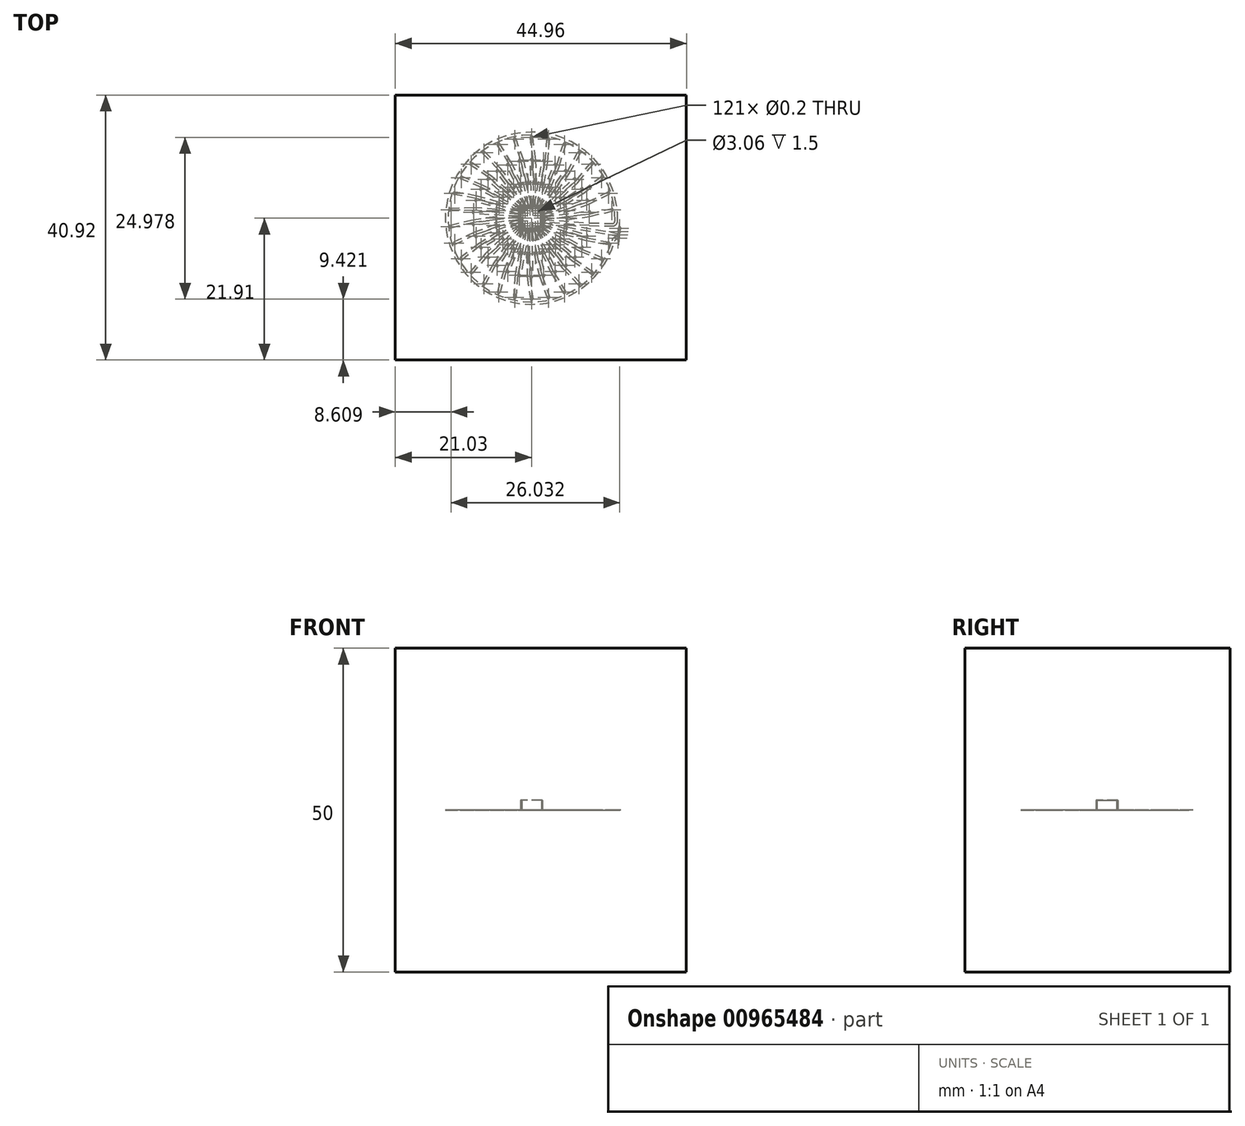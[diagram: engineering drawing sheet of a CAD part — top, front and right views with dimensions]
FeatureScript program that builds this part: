
annotation { "Feature Type Name" : "Feature", "Feature Type Description" : "" }
export const myFeature = defineFeature(function(context is Context, id is Id, definition is map)
    precondition{}
    {
        {
            var Q0;
            Q0=qCreatedBy(makeId("Top.planeOp"), FACE);
            var sketch = newSketch(context, id + "F0", { "sketchPlane" : qUnion([Q0])});
            skLineSegment(sketch, "E0.bottom", {"start": v(-21.03, 19.01) * mm, "end": v(23.93, 19.01) * mm});
            skLineSegment(sketch, "E0.top", {"start": v(-21.03, -21.9) * mm, "end": v(23.93, -21.9) * mm});
            skLineSegment(sketch, "E0.left", {"start": v(-21.03, 19.01) * mm, "end": v(-21.03, -21.9) * mm});
            skLineSegment(sketch, "E0.right", {"start": v(23.93, 19.01) * mm, "end": v(23.93, -21.9) * mm});
            skSolve(sketch);
        }
        {
            var Q0;
            Q0 = qSketchRegion(id + "F0", true);
            extrude(context, id + "F1", {"entities" : qUnion([Q0]), "depth" : 25 * mm, "offsetDistance" : 25 * mm, "hasSecondDirection" : true, "secondDirectionOppositeDirection" : true, "secondDirectionDepth" : 25 * mm});
        }
        {
            assignVariable(context, id + "F2", {"name" : "A", "anyValue" : 12});
        }
        {
            assignVariable(context, id + "F3", {"name" : "ePCB", "anyValue" : 1.5});
        }
        {
            assignVariable(context, id + "F4", {"name" : "eCU", "anyValue" : 0});
        }
        {
            var Q0;
            Q0=qCreatedBy(makeId("Top.planeOp"),FACE);
            var sketch = newSketch(context, id + "F5", { "sketchPlane" : qUnion([Q0])});
            skCircle(sketch, "E1", {"center": v(2, 0) * mm, "radius": 0.1 * mm});
            skCircle(sketch, "E2.1.0", {"center": v(1.96, 0.42) * mm, "radius": 0.1 * mm});
            skPoint(sketch, "E2.center", {"position": v(0, 0) * mm});
            skLineSegment(sketch, "E2.anchor1", {"start": v(0, 0) * mm, "end": v(2, 0) * mm, "construction": true});
            skLineSegment(sketch, "E2.anchor2", {"start": v(0, 0) * mm, "end": v(1.96, 0.42) * mm, "construction": true});
            skLineSegment(sketch, "E3", {"start": v(1.96, 0.42) * mm, "end": v(2, 0) * mm, "construction": true});
            skLineSegment(sketch, "E4", {"start": v(0, 0) * mm, "end": v(1.98, 0.2) * mm, "construction": true});
            skLineSegment(sketch, "E5", {"start": v(1.98, 0.2) * mm, "end": v(8.94, 0.94) * mm, "construction": true});
            skCircle(sketch, "E6", {"center": v(8.94, 0.94) * mm, "radius": 0.1 * mm});
            skCircle(sketch, "E7", {"center": v(2, 0) * mm, "radius": 0.2 * mm});
            skCircle(sketch, "E8", {"center": v(8.94, 0.94) * mm, "radius": 0.2 * mm});
            skCircle(sketch, "E9", {"center": v(1.96, 0.42) * mm, "radius": 0.2 * mm});
            skLineSegment(sketch, "E10", {"start": v(2.03, -0.2) * mm, "end": v(8.97, 0.74) * mm});
            skLineSegment(sketch, "E11", {"start": v(1.97, 0.2) * mm, "end": v(8.91, 1.14) * mm});
            skLineSegment(sketch, "E12", {"start": v(1.97, 0.22) * mm, "end": v(8.95, 0.74) * mm});
            skLineSegment(sketch, "E13", {"start": v(8.92, 1.14) * mm, "end": v(1.94, 0.62) * mm});
            skCircle(sketch, "E14", {"center": v(0, 0) * mm, "radius": 1.7 * mm});
            skLineSegment(sketch, "E15.direction1", {"start": v(2, 0) * mm, "end": v(5.5, 0) * mm, "construction": true});
            skCircle(sketch, "E16.0.1.0", {"center": v(5.5, 0) * mm, "radius": 0.2 * mm});
            skCircle(sketch, "E16.2.1.0", {"center": v(5.5, 0) * mm, "radius": 0.1 * mm});
            skLineSegment(sketch, "E17", {"start": v(8.94, 0.94) * mm, "end": v(12.42, 1.3) * mm, "construction": true});
            skCircle(sketch, "E18", {"center": v(12.42, 1.3) * mm, "radius": 0.1 * mm});
            skCircle(sketch, "E19", {"center": v(12.42, 1.3) * mm, "radius": 0.2 * mm});
            skCircle(sketch, "E20", {"center": v(0, 0) * mm, "radius": 8.99 * mm, "construction": true});
            skLineSegment(sketch, "E21.anchor1", {"start": v(0, 0) * mm, "end": v(5.5, 0) * mm, "construction": true});
            skLineSegment(sketch, "E22", {"start": v(5.5, 0) * mm, "end": v(8.98, 0.47) * mm, "construction": true});
            skCircle(sketch, "E23", {"center": v(8.98, 0.47) * mm, "radius": 0.2 * mm});
            skLineSegment(sketch, "E24", {"start": v(5.53, -0.2) * mm, "end": v(9, 0.27) * mm});
            skLineSegment(sketch, "E25", {"start": v(9, 0.27) * mm, "end": v(12.47, 1.11) * mm});
            skLineSegment(sketch, "E26", {"start": v(5.47, 0.2) * mm, "end": v(8.95, 0.67) * mm});
            skLineSegment(sketch, "E27", {"start": v(8.95, 0.67) * mm, "end": v(12.35, 1.5) * mm});
            skCircle(sketch, "E28.MirrorC", {"center": v(5.38, 1.14) * mm, "radius": 0.2 * mm});
            skLineSegment(sketch, "E29.MirrorCS", {"start": v(5.36, 1.34) * mm, "end": v(8.86, 1.6) * mm});
            skLineSegment(sketch, "E30.MirrorCS", {"start": v(5.4, 0.94) * mm, "end": v(8.9, 1.2) * mm});
            skLineSegment(sketch, "E31.MirrorCS", {"start": v(8.86, 1.6) * mm, "end": v(12.43, 1.5) * mm});
            skLineSegment(sketch, "E32.MirrorCS", {"start": v(8.9, 1.2) * mm, "end": v(12.39, 1.1) * mm});
            skCircle(sketch, "E33.MirrorC", {"center": v(5.38, 1.14) * mm, "radius": 0.1 * mm});
            skLineSegment(sketch, "E34.MirrorCS", {"start": v(2.03, 0.2) * mm, "end": v(8.97, -0.74) * mm});
            skLineSegment(sketch, "E35.MirrorCS", {"start": v(1.97, -0.2) * mm, "end": v(8.91, -1.14) * mm});
            skCircle(sketch, "E36.MirrorC", {"center": v(8.94, -0.94) * mm, "radius": 0.2 * mm});
            skLineSegment(sketch, "E37", {"start": v(2, 0) * mm, "end": v(8.94, -0.94) * mm, "construction": true});
            skCircle(sketch, "E38.MirrorC", {"center": v(8.94, -0.94) * mm, "radius": 0.1 * mm});
            skCircle(sketch, "E39", {"center": v(8.98, 0.47) * mm, "radius": 0.1 * mm});
            skCircle(sketch, "E40.MirrorC", {"center": v(1.96, -0.42) * mm, "radius": 0.2 * mm});
            skCircle(sketch, "E41.MirrorC", {"center": v(1.96, -0.42) * mm, "radius": 0.1 * mm});
            skLineSegment(sketch, "E42.MirrorCS", {"start": v(8.92, -1.14) * mm, "end": v(1.94, -0.62) * mm});
            skLineSegment(sketch, "E43.MirrorCS", {"start": v(1.97, -0.22) * mm, "end": v(8.95, -0.74) * mm});
            skCircle(sketch, "E44.MirrorC", {"center": v(5.38, -1.14) * mm, "radius": 0.2 * mm});
            skCircle(sketch, "E45.MirrorC", {"center": v(5.38, -1.14) * mm, "radius": 0.1 * mm});
            skCircle(sketch, "E46.MirrorC", {"center": v(8.88, 1.4) * mm, "radius": 0.2 * mm});
            skCircle(sketch, "E47.MirrorC", {"center": v(8.88, 1.4) * mm, "radius": 0.1 * mm});
            skLineSegment(sketch, "E48", {"start": v(8.94, -0.94) * mm, "end": v(13.21, -1.52) * mm, "construction": true});
            skCircle(sketch, "E49", {"center": v(0, 0) * mm, "radius": 13.7 * mm, "construction": true});
            skCircle(sketch, "E50", {"center": v(13.7, 0) * mm, "radius": 0.1 * mm});
            skCircle(sketch, "E51", {"center": v(13.7, 0) * mm, "radius": 0.2 * mm});
            skCircle(sketch, "E52.1.0", {"center": v(13.7, -0.52) * mm, "radius": 0.2 * mm});
            skCircle(sketch, "E52.1.1", {"center": v(13.7, -0.52) * mm, "radius": 0.1 * mm});
            skCircle(sketch, "E52.2.0", {"center": v(13.66, -1.04) * mm, "radius": 0.2 * mm});
            skCircle(sketch, "E52.2.1", {"center": v(13.66, -1.04) * mm, "radius": 0.1 * mm});
            skCircle(sketch, "E52.3.0", {"center": v(13.61, -1.55) * mm, "radius": 0.2 * mm});
            skCircle(sketch, "E52.3.1", {"center": v(13.61, -1.55) * mm, "radius": 0.1 * mm});
            skCircle(sketch, "E52.4.0", {"center": v(13.54, -2.06) * mm, "radius": 0.2 * mm});
            skCircle(sketch, "E52.4.1", {"center": v(13.54, -2.06) * mm, "radius": 0.1 * mm});
            skCircle(sketch, "E52.5.0", {"center": v(13.46, -2.57) * mm, "radius": 0.2 * mm});
            skCircle(sketch, "E52.5.1", {"center": v(13.46, -2.57) * mm, "radius": 0.1 * mm});
            skCircle(sketch, "E52.6.0", {"center": v(13.35, -3.08) * mm, "radius": 0.2 * mm});
            skCircle(sketch, "E52.6.1", {"center": v(13.35, -3.08) * mm, "radius": 0.1 * mm});
            skLineSegment(sketch, "E52.anchor1", {"start": v(0, 0) * mm, "end": v(13.7, 0) * mm, "construction": true});
            skLineSegment(sketch, "E52.anchor2", {"start": v(0, 0) * mm, "end": v(13.35, -3.08) * mm, "construction": true});
            skArc(sketch, "E53", {"start": v(12.82, -3.56) * mm, "mid": v(12.94, -3.07) * mm, "end": v(13.05, -2.58) * mm});
            skArc(sketch, "E54", {"start": v(13.3, -0.44) * mm, "mid": v(-13.15, 2.01) * mm, "end": v(12.82, -3.56) * mm});
            skPoint(sketch, "E55.visualSharp", {"position": v(13.3, -0.24) * mm});
            skLineSegment(sketch, "E56", {"start": v(5.5, 0.2) * mm, "end": v(12.49, 0.2) * mm});
            skLineSegment(sketch, "E57", {"start": v(5.5, -0.2) * mm, "end": v(12.49, -0.2) * mm});
            skArc(sketch, "E58.filletArc", {"start": v(12.49, 0.2) * mm, "mid": v(12.78, 0.32) * mm, "end": v(12.89, 0.62) * mm});
            skArc(sketch, "E59.filletArc", {"start": v(12.49, -0.2) * mm, "mid": v(13.06, 0.05) * mm, "end": v(13.28, 0.64) * mm});
            skLineSegment(sketch, "E60", {"start": v(13.37, -2.88) * mm, "end": v(13.4, -2.89) * mm});
            skLineSegment(sketch, "E61", {"start": v(13.3, -3.27) * mm, "end": v(13.3, -3.28) * mm});
            skArc(sketch, "E62.filletArc", {"start": v(13.3, -3.27) * mm, "mid": v(13, -3.32) * mm, "end": v(12.82, -3.56) * mm});
            skArc(sketch, "E63.filletArc", {"start": v(13.37, -2.88) * mm, "mid": v(12.79, -2.98) * mm, "end": v(12.43, -3.45) * mm});
            skLineSegment(sketch, "E64", {"start": v(5.41, -0.95) * mm, "end": v(13.5, -2.38) * mm});
            skLineSegment(sketch, "E65", {"start": v(5.34, -1.34) * mm, "end": v(13.42, -2.77) * mm});
            skLineSegment(sketch, "E66", {"start": v(13.55, -1.86) * mm, "end": v(13.57, -1.87) * mm});
            skLineSegment(sketch, "E67", {"start": v(13.5, -2.26) * mm, "end": v(13.52, -2.26) * mm});
            skArc(sketch, "E68", {"start": v(12.89, -0.42) * mm, "mid": v(-12.81, 1.4) * mm, "end": v(12.65, -2.5) * mm});
            skArc(sketch, "E69.filletArc", {"start": v(13.55, -1.86) * mm, "mid": v(12.97, -2) * mm, "end": v(12.65, -2.5) * mm});
            skArc(sketch, "E70.filletArc", {"start": v(13.5, -2.26) * mm, "mid": v(13.2, -2.33) * mm, "end": v(13.05, -2.58) * mm});
            skLineSegment(sketch, "E71", {"start": v(8.94, -0.74) * mm, "end": v(12.48, -0.81) * mm});
            skLineSegment(sketch, "E72", {"start": v(8.94, -1.14) * mm, "end": v(12.48, -1.21) * mm});
            skArc(sketch, "E73.filletArc", {"start": v(12.48, -1.21) * mm, "mid": v(13.04, -1) * mm, "end": v(13.3, -0.44) * mm});
            skArc(sketch, "E74.filletArc", {"start": v(12.48, -0.81) * mm, "mid": v(12.76, -0.7) * mm, "end": v(12.89, -0.42) * mm});
            skLineSegment(sketch, "E75", {"start": v(8.97, -0.74) * mm, "end": v(13.64, -1.35) * mm});
            skLineSegment(sketch, "E76", {"start": v(8.91, -1.14) * mm, "end": v(13.59, -1.75) * mm});
            skCircle(sketch, "E77", {"center": v(0, 0) * mm, "radius": 1.53 * mm});
            skSolve(sketch);
        }
        {
            var Q0;
            Q0=sQuery(id+"F5.wireOp",EDGE,"E2.1.0");
            var Q1;
            Q1=sQuery(id+"F5.wireOp",EDGE,"E1");
            var Q2;
            Q2=sQuery(id+"F5.wireOp",EDGE,"E6");
            var Q3;
            Q3=sQuery(id+"F5.wireOp",EDGE,"E33.MirrorC");
            var Q4;
            Q4=sQuery(id+"F5.wireOp",EDGE,"E16.2.1.0");
            var Q5;
            Q5=sQuery(id+"F5.wireOp",EDGE,"E18");
            var Q6;
            Q6=sQuery(id+"F5.wireOp",EDGE,"E52.3.1");
            var Q7;
            Q7=sQuery(id+"F5.wireOp",EDGE,"E52.4.1");
            var Q8;
            Q8=sQuery(id+"F5.wireOp",EDGE,"E52.5.1");
            var Q9;
            Q9=sQuery(id+"F5.wireOp",EDGE,"E52.6.1");
            extrude(context, id + "F6", {"bodyType" : ExtendedToolBodyType.SURFACE, "surfaceEntities" : qUnion([Q0, Q1, Q2, Q3, Q4, Q5, Q6, Q7, Q8, Q9]), "depth" : (getVariable(context, 'ePCB')) * mm, "offsetDistance" : 25 * mm});
        }
        {
            var Q0;
            {var subQ0=sQuery(id+"F5.wireOp",EDGE,"E10");Q0=makeQuery(id+"F5.imprint","IMPRINT",FACE,{"disambiguationData":[TD([[makeQuery(id+"F5.imprint","IMPRINT",EDGE,{"derivedFrom":subQ0}),1.0]])]});}
            var Q1;
            {var subQ0=sQuery(id+"F5.wireOp",EDGE,"E11");var subQ1=sQuery(id+"F5.wireOp",EDGE,"E8");var subQ2=makeQuery(id+"F5.imprint","INTERSECT",VERTEX,{"derivedFrom":[subQ1,subQ0]});Q1=makeQuery(id+"F5.imprint","IMPRINT",FACE,{"disambiguationData":[TD([[makeQuery(id+"F5.imprint","IMPRINT",EDGE,{"disambiguationData":[TD([[subQ2,-1.0]])],"derivedFrom":subQ1}),-1.0]])]});}
            var Q2;
            Q2=makeQuery(id+"F5.imprint","IMPRINT",FACE,{"disambiguationData":[TD([[makeQuery(id+"F5.imprint","IMPRINT",EDGE,{"derivedFrom":sQuery(id+"F5.wireOp",EDGE,"E6")}),-1.0]])]});
            var Q3;
            Q3=makeQuery(id+"F5.imprint","IMPRINT",FACE,{"disambiguationData":[TD([[makeQuery(id+"F5.imprint","IMPRINT",EDGE,{"derivedFrom":sQuery(id+"F5.wireOp",EDGE,"E1")}),-1.0]])]});
            var Q4;
            {var subQ0=sQuery(id+"F5.wireOp",EDGE,"E24");Q4=makeQuery(id+"F5.imprint","IMPRINT",FACE,{"disambiguationData":[TD([[makeQuery(id+"F5.imprint","IMPRINT",EDGE,{"derivedFrom":subQ0}),1.0]])]});}
            var Q5;
            {var subQ0=sQuery(id+"F5.wireOp",EDGE,"E25");var subQ1=sQuery(id+"F5.wireOp",EDGE,"E23");var subQ4=makeQuery(id+"F5.imprint","INTERSECT",VERTEX,{"derivedFrom":[subQ1,subQ0]});Q5=makeQuery(id+"F5.imprint","IMPRINT",FACE,{"disambiguationData":[TD([[makeQuery(id+"F5.imprint","IMPRINT",EDGE,{"disambiguationData":[TD([[subQ4,-1.0]])],"derivedFrom":subQ1}),1.0]])]});}
            var Q6;
            {var subQ0=sQuery(id+"F5.wireOp",EDGE,"E25");var subQ1=sQuery(id+"F5.wireOp",EDGE,"E19");var subQ2=makeQuery(id+"F5.imprint","INTERSECT",VERTEX,{"derivedFrom":[subQ1,subQ0]});Q6=makeQuery(id+"F5.imprint","IMPRINT",FACE,{"disambiguationData":[TD([[makeQuery(id+"F5.imprint","IMPRINT",EDGE,{"disambiguationData":[TD([[subQ2,1.0]])],"derivedFrom":subQ1}),-1.0]])]});}
            var Q7;
            {var subQ0=sQuery(id+"F5.wireOp",EDGE,"E27");var subQ1=sQuery(id+"F5.wireOp",EDGE,"E19");var subQ2=makeQuery(id+"F5.imprint","INTERSECT",VERTEX,{"derivedFrom":[subQ1,subQ0]});Q7=makeQuery(id+"F5.imprint","IMPRINT",FACE,{"disambiguationData":[TD([[makeQuery(id+"F5.imprint","IMPRINT",EDGE,{"disambiguationData":[TD([[subQ2,-1.0]])],"derivedFrom":subQ1}),-1.0]])]});}
            var Q8;
            Q8=makeQuery(id+"F5.imprint","IMPRINT",FACE,{"disambiguationData":[TD([[makeQuery(id+"F5.imprint","IMPRINT",EDGE,{"derivedFrom":sQuery(id+"F5.wireOp",EDGE,"E18")}),-1.0]])]});
            var Q9;
            Q9=makeQuery(id+"F5.imprint","IMPRINT",FACE,{"disambiguationData":[TD([[makeQuery(id+"F5.imprint","IMPRINT",EDGE,{"derivedFrom":sQuery(id+"F5.wireOp",EDGE,"E16.2.1.0")}),-1.0]])]});
            var Q10;
            {var subQ0=sQuery(id+"F5.wireOp",EDGE,"E11");var subQ1=sQuery(id+"F5.wireOp",EDGE,"E7");var subQ2=makeQuery(id+"F5.imprint","INTERSECT",VERTEX,{"derivedFrom":[subQ1,subQ0]});Q10=makeQuery(id+"F5.imprint","IMPRINT",FACE,{"disambiguationData":[TD([[makeQuery(id+"F5.imprint","IMPRINT",EDGE,{"disambiguationData":[TD([[subQ2,1.0]])],"derivedFrom":subQ1}),-1.0]])]});}
            var Q11;
            {var subQ0=sQuery(id+"F5.wireOp",EDGE,"E26");Q11=makeQuery(id+"F5.imprint","IMPRINT",FACE,{"disambiguationData":[TD([[makeQuery(id+"F5.imprint","IMPRINT",EDGE,{"derivedFrom":subQ0}),-1.0]])]});}
            var Q12;
            Q12=makeQuery(id+"F5.imprint","IMPRINT",FACE,{"disambiguationData":[TD([[makeQuery(id+"F5.imprint","IMPRINT",EDGE,{"derivedFrom":sQuery(id+"F5.wireOp",EDGE,"E39")}),1.0]])]});
            var Q13;
            Q13=makeQuery(id+"F5.imprint","IMPRINT",FACE,{"disambiguationData":[TD([[makeQuery(id+"F5.imprint","IMPRINT",EDGE,{"derivedFrom":sQuery(id+"F5.wireOp",EDGE,"E41.MirrorC")}),1.0]])]});
            var Q14;
            {var subQ0=sQuery(id+"F5.wireOp",EDGE,"E42.MirrorCS");Q14=makeQuery(id+"F5.imprint","IMPRINT",FACE,{"disambiguationData":[TD([[makeQuery(id+"F5.imprint","IMPRINT",EDGE,{"derivedFrom":subQ0}),-1.0]])]});}
            var Q15;
            {var subQ0=sQuery(id+"F5.wireOp",EDGE,"E36.MirrorC");var subQ1=sQuery(id+"F5.wireOp",EDGE,"E35.MirrorCS");var subQ2=makeQuery(id+"F5.imprint","INTERSECT",VERTEX,{"derivedFrom":[subQ1,subQ0]});Q15=makeQuery(id+"F5.imprint","IMPRINT",FACE,{"disambiguationData":[TD([[makeQuery(id+"F5.imprint","IMPRINT",EDGE,{"disambiguationData":[TD([[subQ2,1.0]])],"derivedFrom":subQ1}),1.0]])]});}
            var Q16;
            Q16=makeQuery(id+"F5.imprint","IMPRINT",FACE,{"disambiguationData":[TD([[makeQuery(id+"F5.imprint","IMPRINT",EDGE,{"derivedFrom":sQuery(id+"F5.wireOp",EDGE,"E38.MirrorC")}),1.0]])]});
            var Q17;
            Q17=makeQuery(id+"F5.imprint","IMPRINT",FACE,{"disambiguationData":[TD([[makeQuery(id+"F5.imprint","IMPRINT",EDGE,{"derivedFrom":sQuery(id+"F5.wireOp",EDGE,"E38.MirrorC")}),-1.0]])]});
            var Q18;
            {var subQ0=sQuery(id+"F5.wireOp",EDGE,"fd1f0fe6-7b20-4042-ae50-64046cc540670.MirrorCS");Q18=makeQuery(id+"F5.imprint","IMPRINT",FACE,{"disambiguationData":[TD([[makeQuery(id+"F5.imprint","IMPRINT",EDGE,{"derivedFrom":subQ0}),-1.0]])]});}
            var Q19;
            Q19=makeQuery(id+"F5.imprint","IMPRINT",FACE,{"disambiguationData":[TD([[makeQuery(id+"F5.imprint","IMPRINT",EDGE,{"derivedFrom":sQuery(id+"F5.wireOp",EDGE,"E45.MirrorC")}),-1.0]])]});
            var Q20;
            Q20=makeQuery(id+"F5.imprint","IMPRINT",FACE,{"disambiguationData":[TD([[makeQuery(id+"F5.imprint","IMPRINT",EDGE,{"derivedFrom":sQuery(id+"F5.wireOp",EDGE,"3a97ee7c-a2b4-491a-8cde-c9a1e66886190.MirrorC")}),-1.0]])]});
            var Q21;
            Q21=makeQuery(id+"F5.imprint","IMPRINT",FACE,{"disambiguationData":[TD([[makeQuery(id+"F5.imprint","IMPRINT",EDGE,{"derivedFrom":sQuery(id+"F5.wireOp",EDGE,"3a97ee7c-a2b4-491a-8cde-c9a1e66886190.MirrorC")}),1.0]])]});
            var Q22;
            {var subQ5=sQuery(id+"F5.wireOp",EDGE,"E36.MirrorC");var subQ6=sQuery(id+"F5.wireOp",EDGE,"E35.MirrorCS");var subQ7=makeQuery(id+"F5.imprint","INTERSECT",VERTEX,{"derivedFrom":[subQ6,subQ5]});Q22=makeQuery(id+"F5.imprint","IMPRINT",FACE,{"disambiguationData":[TD([[makeQuery(id+"F5.imprint","IMPRINT",EDGE,{"disambiguationData":[TD([[subQ7,1.0]])],"derivedFrom":subQ6}),-1.0]])]});}
            var Q23;
            {var subQ0=sQuery(id+"F5.wireOp",EDGE,"E60");Q23=makeQuery(id+"F5.imprint","IMPRINT",FACE,{"disambiguationData":[TD([[makeQuery(id+"F5.imprint","IMPRINT",EDGE,{"derivedFrom":subQ0}),-1.0]])]});}
            var Q24;
            Q24=makeQuery(id+"F5.imprint","IMPRINT",FACE,{"disambiguationData":[TD([[makeQuery(id+"F5.imprint","IMPRINT",EDGE,{"derivedFrom":sQuery(id+"F5.wireOp",EDGE,"E52.6.1")}),-1.0]])]});
            var Q25;
            {var subQ0=sQuery(id+"F5.wireOp",EDGE,"E72");Q25=makeQuery(id+"F5.imprint","IMPRINT",FACE,{"disambiguationData":[TD([[makeQuery(id+"F5.imprint","IMPRINT",EDGE,{"derivedFrom":subQ0}),1.0]])]});}
            var Q26;
            {var subQ0=sQuery(id+"F5.wireOp",EDGE,"E74.filletArc");Q26=makeQuery(id+"F5.imprint","IMPRINT",FACE,{"disambiguationData":[TD([[makeQuery(id+"F5.imprint","IMPRINT",EDGE,{"derivedFrom":subQ0}),-1.0]])]});}
            var Q27;
            {var subQ6=sQuery(id+"F5.wireOp",EDGE,"E54");var subQ8=sQuery(id+"F5.wireOp",EDGE,"E59.filletArc");var subQ9=makeQuery(id+"F5.imprint","INTERSECT",VERTEX,{"derivedFrom":[subQ6,subQ8]});Q27=makeQuery(id+"F5.imprint","IMPRINT",FACE,{"disambiguationData":[TD([[makeQuery(id+"F5.imprint","IMPRINT",EDGE,{"disambiguationData":[TD([[subQ9,1.0]])],"derivedFrom":subQ8}),1.0]])]});}
            var Q28;
            {var subQ5=sQuery(id+"F5.wireOp",EDGE,"E44.MirrorC");var subQ7=sQuery(id+"F5.wireOp",EDGE,"E64");var subQ9=makeQuery(id+"F5.imprint","INTERSECT",VERTEX,{"derivedFrom":[subQ5,subQ7]});Q28=makeQuery(id+"F5.imprint","IMPRINT",FACE,{"disambiguationData":[TD([[makeQuery(id+"F5.imprint","IMPRINT",EDGE,{"disambiguationData":[TD([[subQ9,1.0]])],"derivedFrom":subQ5}),-1.0]])]});}
            var Q29;
            {var subQ1=sQuery(id+"F5.wireOp",EDGE,"E53");var subQ8=sQuery(id+"F5.wireOp",EDGE,"E70.filletArc");var subQ11=makeQuery(id+"F5.imprint","INTERSECT",VERTEX,{"derivedFrom":[subQ1,subQ8]});Q29=makeQuery(id+"F5.imprint","IMPRINT",FACE,{"disambiguationData":[TD([[makeQuery(id+"F5.imprint","IMPRINT",EDGE,{"disambiguationData":[TD([[subQ11,1.0]])],"derivedFrom":subQ1}),1.0]])]});}
            var Q30;
            {var subQ1=sQuery(id+"F5.wireOp",EDGE,"E52.5.0");var subQ7=sQuery(id+"F5.wireOp",EDGE,"E64");var subQ9=makeQuery(id+"F5.imprint","INTERSECT",VERTEX,{"derivedFrom":[subQ1,subQ7]});Q30=makeQuery(id+"F5.imprint","IMPRINT",FACE,{"disambiguationData":[TD([[makeQuery(id+"F5.imprint","IMPRINT",EDGE,{"disambiguationData":[TD([[subQ9,-1.0]])],"derivedFrom":subQ1}),-1.0]])]});}
            var Q31;
            Q31=makeQuery(id+"F5.imprint","IMPRINT",FACE,{"disambiguationData":[TD([[makeQuery(id+"F5.imprint","IMPRINT",EDGE,{"derivedFrom":sQuery(id+"F5.wireOp",EDGE,"E52.5.1")}),-1.0]])]});
            var Q32;
            Q32=makeQuery(id+"F5.imprint","IMPRINT",FACE,{"disambiguationData":[TD([[makeQuery(id+"F5.imprint","IMPRINT",EDGE,{"derivedFrom":sQuery(id+"F5.wireOp",EDGE,"E52.4.1")}),-1.0]])]});
            var Q33;
            Q33=makeQuery(id+"F5.imprint","IMPRINT",FACE,{"disambiguationData":[TD([[makeQuery(id+"F5.imprint","IMPRINT",EDGE,{"derivedFrom":sQuery(id+"F5.wireOp",EDGE,"E52.3.1")}),-1.0]])]});
            extrude(context, id + "F7", {"entities" : qUnion([Q0, Q1, Q2, Q3, Q4, Q5, Q6, Q7, Q8, Q9, Q10, Q11, Q12, Q13, Q14, Q15, Q16, Q17, Q18, Q19, Q20, Q21, Q22, Q23, Q24, Q25, Q26, Q27, Q28, Q29, Q30, Q31, Q32, Q33]), "oppositeDirection" : true, "depth" : (getVariable(context, 'eCU')) * mm, "offsetDistance" : 25 * mm});
        }
        {
            var Q0;
            Q0=makeQuery(id+"F5.imprint","IMPRINT",FACE,{"disambiguationData":[TD([[makeQuery(id+"F5.imprint","IMPRINT",EDGE,{"derivedFrom":sQuery(id+"F5.wireOp",EDGE,"E2.1.0")}),-1.0]])]});
            var Q1;
            {var subQ7=sQuery(id+"F5.wireOp",EDGE,"E13");Q1=makeQuery(id+"F5.imprint","IMPRINT",FACE,{"disambiguationData":[TD([[makeQuery(id+"F5.imprint","IMPRINT",EDGE,{"derivedFrom":subQ7}),1.0]])]});}
            var Q2;
            {var subQ0=sQuery(id+"F5.wireOp",EDGE,"E11");var subQ1=sQuery(id+"F5.wireOp",EDGE,"E8");var subQ2=makeQuery(id+"F5.imprint","INTERSECT",VERTEX,{"derivedFrom":[subQ1,subQ0]});Q2=makeQuery(id+"F5.imprint","IMPRINT",FACE,{"disambiguationData":[TD([[makeQuery(id+"F5.imprint","IMPRINT",EDGE,{"disambiguationData":[TD([[subQ2,-1.0]])],"derivedFrom":subQ1}),-1.0]])]});}
            var Q3;
            Q3=makeQuery(id+"F5.imprint","IMPRINT",FACE,{"disambiguationData":[TD([[makeQuery(id+"F5.imprint","IMPRINT",EDGE,{"derivedFrom":sQuery(id+"F5.wireOp",EDGE,"E6")}),-1.0]])]});
            var Q4;
            {var subQ0=sQuery(id+"F5.wireOp",EDGE,"E29.MirrorCS");Q4=makeQuery(id+"F5.imprint","IMPRINT",FACE,{"disambiguationData":[TD([[makeQuery(id+"F5.imprint","IMPRINT",EDGE,{"derivedFrom":subQ0}),-1.0]])]});}
            var Q5;
            Q5=makeQuery(id+"F5.imprint","IMPRINT",FACE,{"disambiguationData":[TD([[makeQuery(id+"F5.imprint","IMPRINT",EDGE,{"derivedFrom":sQuery(id+"F5.wireOp",EDGE,"E33.MirrorC")}),1.0]])]});
            var Q6;
            {var subQ0=sQuery(id+"F5.wireOp",EDGE,"E27");var subQ1=sQuery(id+"F5.wireOp",EDGE,"E19");var subQ2=makeQuery(id+"F5.imprint","INTERSECT",VERTEX,{"derivedFrom":[subQ1,subQ0]});Q6=makeQuery(id+"F5.imprint","IMPRINT",FACE,{"disambiguationData":[TD([[makeQuery(id+"F5.imprint","IMPRINT",EDGE,{"disambiguationData":[TD([[subQ2,-1.0]])],"derivedFrom":subQ1}),-1.0]])]});}
            var Q7;
            Q7=makeQuery(id+"F5.imprint","IMPRINT",FACE,{"disambiguationData":[TD([[makeQuery(id+"F5.imprint","IMPRINT",EDGE,{"derivedFrom":sQuery(id+"F5.wireOp",EDGE,"E18")}),-1.0]])]});
            var Q8;
            {var subQ5=sQuery(id+"F5.wireOp",EDGE,"E35.MirrorCS");Q8=makeQuery(id+"F5.imprint","IMPRINT",FACE,{"disambiguationData":[TD([[makeQuery(id+"F5.imprint","IMPRINT",EDGE,{"derivedFrom":subQ5}),1.0]])]});}
            var Q9;
            {var subQ0=sQuery(id+"F5.wireOp",EDGE,"E10");var subQ1=sQuery(id+"F5.wireOp",EDGE,"E7");var subQ2=makeQuery(id+"F5.imprint","INTERSECT",VERTEX,{"derivedFrom":[subQ1,subQ0]});Q9=makeQuery(id+"F5.imprint","IMPRINT",FACE,{"disambiguationData":[TD([[makeQuery(id+"F5.imprint","IMPRINT",EDGE,{"disambiguationData":[TD([[subQ2,-1.0]])],"derivedFrom":subQ1}),-1.0]])]});}
            var Q10;
            Q10=makeQuery(id+"F5.imprint","IMPRINT",FACE,{"disambiguationData":[TD([[makeQuery(id+"F5.imprint","IMPRINT",EDGE,{"derivedFrom":sQuery(id+"F5.wireOp",EDGE,"E1")}),-1.0]])]});
            var Q11;
            Q11=makeQuery(id+"F5.imprint","IMPRINT",FACE,{"disambiguationData":[TD([[makeQuery(id+"F5.imprint","IMPRINT",EDGE,{"derivedFrom":sQuery(id+"F5.wireOp",EDGE,"E38.MirrorC")}),1.0]])]});
            var Q12;
            Q12=makeQuery(id+"F5.imprint","IMPRINT",FACE,{"disambiguationData":[TD([[makeQuery(id+"F5.imprint","IMPRINT",EDGE,{"derivedFrom":sQuery(id+"F5.wireOp",EDGE,"05892bbe-deb6-4acd-8c1b-d11f433cfc480.MirrorC")}),1.0]])]});
            var Q13;
            {var subQ0=sQuery(id+"F5.wireOp",EDGE,"e91d1a98-e26d-4999-89b6-a410c2d17d9b0.MirrorCS");Q13=makeQuery(id+"F5.imprint","IMPRINT",FACE,{"disambiguationData":[TD([[makeQuery(id+"F5.imprint","IMPRINT",EDGE,{"derivedFrom":subQ0}),1.0]])]});}
            var Q14;
            {var subQ0=sQuery(id+"F5.wireOp",EDGE,"E24");var subQ1=sQuery(id+"F5.wireOp",EDGE,"E16.0.1.0");var subQ2=makeQuery(id+"F5.imprint","INTERSECT",VERTEX,{"derivedFrom":[subQ1,subQ0]});Q14=makeQuery(id+"F5.imprint","IMPRINT",FACE,{"disambiguationData":[TD([[makeQuery(id+"F5.imprint","IMPRINT",EDGE,{"disambiguationData":[TD([[subQ2,-1.0]])],"derivedFrom":subQ1}),-1.0]])]});}
            var Q15;
            Q15=makeQuery(id+"F5.imprint","IMPRINT",FACE,{"disambiguationData":[TD([[makeQuery(id+"F5.imprint","IMPRINT",EDGE,{"derivedFrom":sQuery(id+"F5.wireOp",EDGE,"E16.2.1.0")}),-1.0]])]});
            var Q16;
            {var subQ1=sQuery(id+"F5.wireOp",EDGE,"E7");var subQ8=sQuery(id+"F5.wireOp",EDGE,"E10");var subQ10=makeQuery(id+"F5.imprint","INTERSECT",VERTEX,{"derivedFrom":[subQ1,subQ8]});Q16=makeQuery(id+"F5.imprint","IMPRINT",FACE,{"disambiguationData":[TD([[makeQuery(id+"F5.imprint","IMPRINT",EDGE,{"disambiguationData":[TD([[subQ10,1.0]])],"derivedFrom":subQ1}),-1.0]])]});}
            var Q17;
            {var subQ1=sQuery(id+"F5.wireOp",EDGE,"E19");var subQ5=sQuery(id+"F5.wireOp",EDGE,"E27");var subQ6=makeQuery(id+"F5.imprint","INTERSECT",VERTEX,{"derivedFrom":[subQ1,subQ5]});Q17=makeQuery(id+"F5.imprint","IMPRINT",FACE,{"disambiguationData":[TD([[makeQuery(id+"F5.imprint","IMPRINT",EDGE,{"disambiguationData":[TD([[subQ6,1.0]])],"derivedFrom":subQ1}),-1.0]])]});}
            var Q18;
            Q18=makeQuery(id+"F5.imprint","IMPRINT",FACE,{"disambiguationData":[TD([[makeQuery(id+"F5.imprint","IMPRINT",EDGE,{"derivedFrom":sQuery(id+"F5.wireOp",EDGE,"E47.MirrorC")}),1.0]])]});
            var Q19;
            Q19=makeQuery(id+"F5.imprint","IMPRINT",FACE,{"disambiguationData":[TD([[makeQuery(id+"F5.imprint","IMPRINT",EDGE,{"derivedFrom":sQuery(id+"F5.wireOp",EDGE,"E47.MirrorC")}),-1.0]])]});
            var Q20;
            Q20=makeQuery(id+"F5.imprint","IMPRINT",FACE,{"disambiguationData":[TD([[makeQuery(id+"F5.imprint","IMPRINT",EDGE,{"derivedFrom":sQuery(id+"F5.wireOp",EDGE,"05892bbe-deb6-4acd-8c1b-d11f433cfc480.MirrorC")}),-1.0]])]});
            var Q21;
            Q21=makeQuery(id+"F5.imprint","IMPRINT",FACE,{"disambiguationData":[TD([[makeQuery(id+"F5.imprint","IMPRINT",EDGE,{"derivedFrom":sQuery(id+"F5.wireOp",EDGE,"E38.MirrorC")}),-1.0]])]});
            var Q22;
            {var subQ0=sQuery(id+"F5.wireOp",EDGE,"E57");Q22=makeQuery(id+"F5.imprint","IMPRINT",FACE,{"disambiguationData":[TD([[makeQuery(id+"F5.imprint","IMPRINT",EDGE,{"derivedFrom":subQ0}),1.0]])]});}
            var Q23;
            {var subQ6=sQuery(id+"F5.wireOp",EDGE,"E54");var subQ8=sQuery(id+"F5.wireOp",EDGE,"E59.filletArc");var subQ9=makeQuery(id+"F5.imprint","INTERSECT",VERTEX,{"derivedFrom":[subQ6,subQ8]});Q23=makeQuery(id+"F5.imprint","IMPRINT",FACE,{"disambiguationData":[TD([[makeQuery(id+"F5.imprint","IMPRINT",EDGE,{"disambiguationData":[TD([[subQ9,1.0]])],"derivedFrom":subQ8}),1.0]])]});}
            var Q24;
            {var subQ0=sQuery(id+"F5.wireOp",EDGE,"E63.filletArc");var subQ1=sQuery(id+"F5.wireOp",EDGE,"E53");var subQ2=makeQuery(id+"F5.imprint","INTERSECT",VERTEX,{"derivedFrom":[subQ1,subQ0]});Q24=makeQuery(id+"F5.imprint","IMPRINT",FACE,{"disambiguationData":[TD([[makeQuery(id+"F5.imprint","IMPRINT",EDGE,{"disambiguationData":[TD([[subQ2,-1.0]])],"derivedFrom":subQ1}),1.0]])]});}
            var Q25;
            {var subQ1=sQuery(id+"F5.wireOp",EDGE,"E53");var subQ8=sQuery(id+"F5.wireOp",EDGE,"E70.filletArc");var subQ11=makeQuery(id+"F5.imprint","INTERSECT",VERTEX,{"derivedFrom":[subQ1,subQ8]});Q25=makeQuery(id+"F5.imprint","IMPRINT",FACE,{"disambiguationData":[TD([[makeQuery(id+"F5.imprint","IMPRINT",EDGE,{"disambiguationData":[TD([[subQ11,1.0]])],"derivedFrom":subQ1}),1.0]])]});}
            var Q26;
            {var subQ1=sQuery(id+"F5.wireOp",EDGE,"E66");Q26=makeQuery(id+"F5.imprint","IMPRINT",FACE,{"disambiguationData":[TD([[makeQuery(id+"F5.imprint","IMPRINT",EDGE,{"derivedFrom":subQ1}),-1.0]])]});}
            var Q27;
            Q27=makeQuery(id+"F5.imprint","IMPRINT",FACE,{"disambiguationData":[TD([[makeQuery(id+"F5.imprint","IMPRINT",EDGE,{"derivedFrom":sQuery(id+"F5.wireOp",EDGE,"E52.4.1")}),-1.0]])]});
            var Q28;
            {var subQ0=sQuery(id+"F5.wireOp",EDGE,"E72");Q28=makeQuery(id+"F5.imprint","IMPRINT",FACE,{"disambiguationData":[TD([[makeQuery(id+"F5.imprint","IMPRINT",EDGE,{"derivedFrom":subQ0}),1.0]])]});}
            var Q29;
            {var subQ0=sQuery(id+"F5.wireOp",EDGE,"E72");Q29=makeQuery(id+"F5.imprint","IMPRINT",FACE,{"disambiguationData":[TD([[makeQuery(id+"F5.imprint","IMPRINT",EDGE,{"derivedFrom":subQ0}),-1.0]])]});}
            var Q30;
            Q30=makeQuery(id+"F5.imprint","IMPRINT",FACE,{"disambiguationData":[TD([[makeQuery(id+"F5.imprint","IMPRINT",EDGE,{"derivedFrom":sQuery(id+"F5.wireOp",EDGE,"E52.3.1")}),-1.0]])]});
            var Q31;
            Q31=makeQuery(id+"F5.imprint","IMPRINT",FACE,{"disambiguationData":[TD([[makeQuery(id+"F5.imprint","IMPRINT",EDGE,{"derivedFrom":sQuery(id+"F5.wireOp",EDGE,"E52.5.1")}),-1.0]])]});
            var Q32;
            Q32=makeQuery(id+"F5.imprint","IMPRINT",FACE,{"disambiguationData":[TD([[makeQuery(id+"F5.imprint","IMPRINT",EDGE,{"derivedFrom":sQuery(id+"F5.wireOp",EDGE,"E52.6.1")}),-1.0]])]});
            extrude(context, id + "F8", {"entities" : qUnion([Q0, Q1, Q2, Q3, Q4, Q5, Q6, Q7, Q8, Q9, Q10, Q11, Q12, Q13, Q14, Q15, Q16, Q17, Q18, Q19, Q20, Q21, Q22, Q23, Q24, Q25, Q26, Q27, Q28, Q29, Q30, Q31, Q32]), "operationType" : NewBodyOperationType.ADD, "depth" : (getVariable(context, 'ePCB') + getVariable(context, 'eCU')) * mm, "offsetDistance" : 25 * mm, "hasSecondDirection" : true, "secondDirectionOppositeDirection" : false, "secondDirectionDepth" : (getVariable(context, 'ePCB')) * mm});
        }
        {
            var Q0;
            Q0=makeQuery(id+"F5.imprint","IMPRINT",FACE,{"disambiguationData":[TD([[makeQuery(id+"F5.imprint","IMPRINT",EDGE,{"derivedFrom":sQuery(id+"F5.wireOp",EDGE,"E14")}),1.0]])]});
            extrude(context, id + "F9", {"entities" : qUnion([Q0]), "depth" : (getVariable(context, 'ePCB')) * mm, "offsetDistance" : 25 * mm});
        }
        {
            var Q0;
            Q0=makeQuery(id+"F6.opExtrude","SWEPT_BODY",BODY,{"disambiguationData":[OSD([sQuery(id+"F5.wireOp",EDGE,"E2.1.0")])]});
            var Q1;
            Q1=makeQuery(id+"F7.opExtrude","SWEPT_BODY",BODY,{"disambiguationData":[OSD([sQuery(id+"F5.wireOp",EDGE,"E1"),sQuery(id+"F5.wireOp",EDGE,"E6"),sQuery(id+"F5.wireOp",EDGE,"E7"),sQuery(id+"F5.wireOp",EDGE,"E8"),sQuery(id+"F5.wireOp",EDGE,"E10"),sQuery(id+"F5.wireOp",EDGE,"E11")])]});
            var Q2;
            Q2=makeQuery(id+"F6.opExtrude","SWEPT_BODY",BODY,{"disambiguationData":[OSD([sQuery(id+"F5.wireOp",EDGE,"E6")])]});
            var Q3;
            Q3=makeQuery(id+"F6.opExtrude","SWEPT_BODY",BODY,{"disambiguationData":[OSD([sQuery(id+"F5.wireOp",EDGE,"E1")])]});
            var Q4;
            Q4=makeQuery(id+"F8.opExtrude","SWEPT_BODY",BODY,{"disambiguationData":[OSD([sQuery(id+"F5.wireOp",EDGE,"E2.1.0"),sQuery(id+"F5.wireOp",EDGE,"E6"),sQuery(id+"F5.wireOp",EDGE,"E8"),sQuery(id+"F5.wireOp",EDGE,"E9"),sQuery(id+"F5.wireOp",EDGE,"E12"),sQuery(id+"F5.wireOp",EDGE,"E13")])]});
            var Q5;
            Q5=makeQuery(id+"F8.opExtrude","SWEPT_BODY",BODY,{"disambiguationData":[OSD([sQuery(id+"F5.wireOp",EDGE,"E18"),sQuery(id+"F5.wireOp",EDGE,"E19"),sQuery(id+"F5.wireOp",EDGE,"E28.MirrorC"),sQuery(id+"F5.wireOp",EDGE,"E29.MirrorCS"),sQuery(id+"F5.wireOp",EDGE,"E30.MirrorCS"),sQuery(id+"F5.wireOp",EDGE,"E31.MirrorCS"),sQuery(id+"F5.wireOp",EDGE,"E32.MirrorCS"),sQuery(id+"F5.wireOp",EDGE,"E33.MirrorC")])]});
            var Q6;
            Q6=makeQuery(id+"F7.opExtrude","SWEPT_BODY",BODY,{"disambiguationData":[OSD([sQuery(id+"F5.wireOp",EDGE,"E16.0.1.0"),sQuery(id+"F5.wireOp",EDGE,"E16.2.1.0"),sQuery(id+"F5.wireOp",EDGE,"E18"),sQuery(id+"F5.wireOp",EDGE,"E19"),sQuery(id+"F5.wireOp",EDGE,"E24"),sQuery(id+"F5.wireOp",EDGE,"E25"),sQuery(id+"F5.wireOp",EDGE,"E26"),sQuery(id+"F5.wireOp",EDGE,"E27")])]});
            var Q7;
            Q7=makeQuery(id+"F6.opExtrude","SWEPT_BODY",BODY,{"disambiguationData":[OSD([sQuery(id+"F5.wireOp",EDGE,"E18")])]});
            var Q8;
            Q8=makeQuery(id+"F6.opExtrude","SWEPT_BODY",BODY,{"disambiguationData":[OSD([sQuery(id+"F5.wireOp",EDGE,"E16.2.1.0")])]});
            var Q9;
            Q9=makeQuery(id+"F6.opExtrude","SWEPT_BODY",BODY,{"disambiguationData":[OSD([sQuery(id+"F5.wireOp",EDGE,"E33.MirrorC")])]});
            var Q10;
            Q10=makeQuery(id+"F9.opExtrude","CAP_EDGE",EDGE,{"disambiguationData":[OSD([sQuery(id+"F5.wireOp",EDGE,"E14")])],"isStart":false});
            circularPattern(context, id + "F10", {"entities" : qUnion([Q0, Q1, Q2, Q3, Q4, Q5, Q6, Q7, Q8, Q9]), "axis" : qUnion([Q10]), "angle" : (360 - getVariable(context, 'A')) * degree, "instanceCount" : (360 / getVariable(context, 'A')) - 1, "oppositeDirection" : true});
        }
    });
